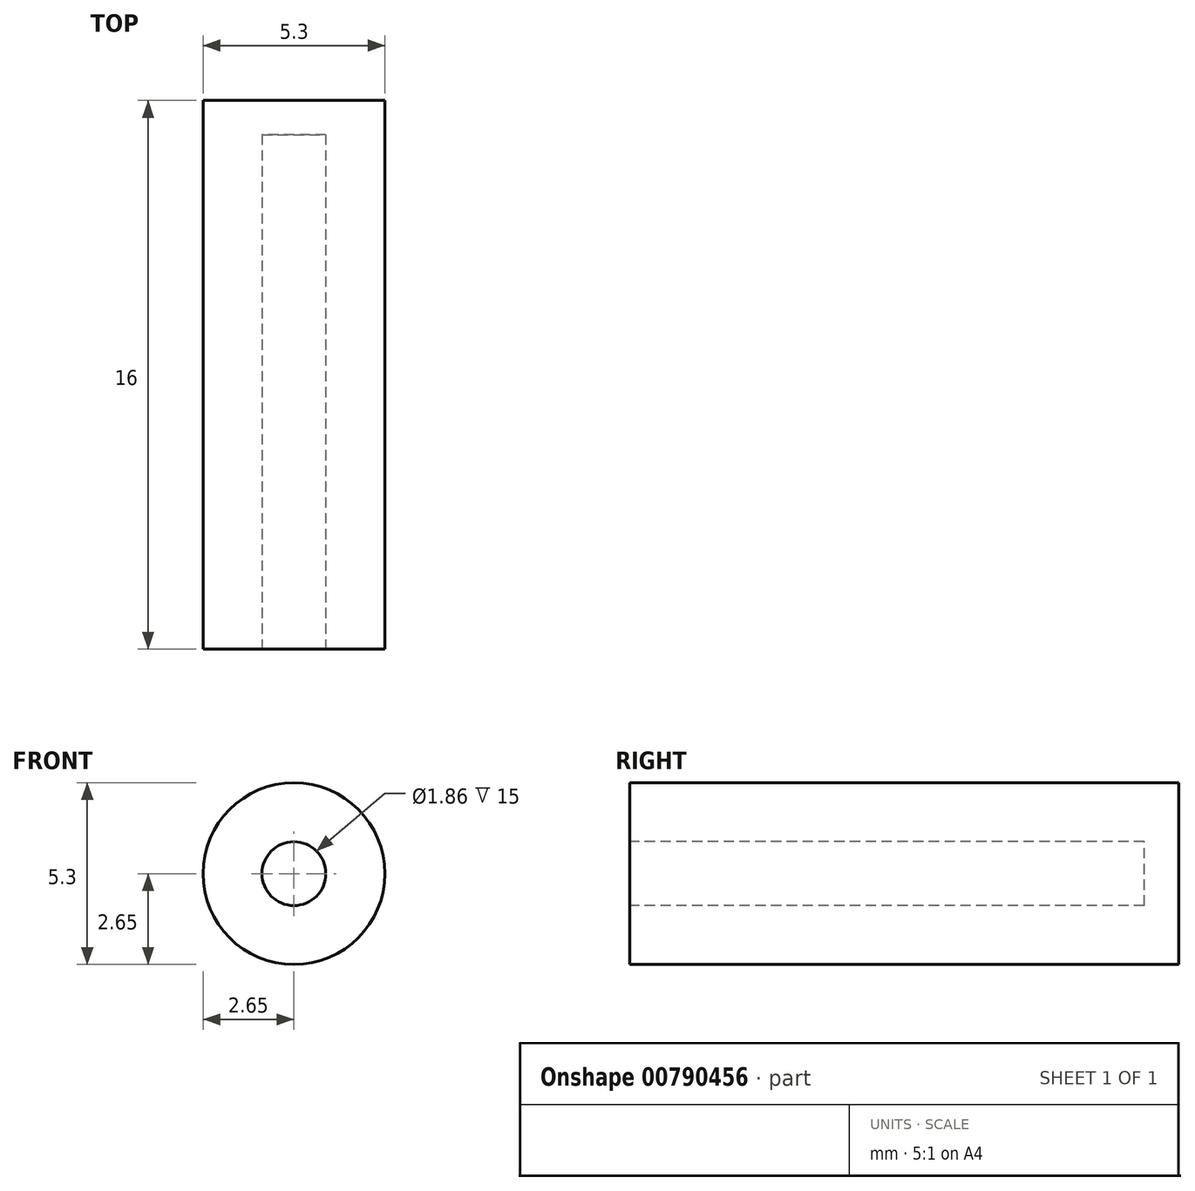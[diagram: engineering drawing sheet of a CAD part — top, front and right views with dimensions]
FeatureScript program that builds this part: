
annotation { "Feature Type Name" : "Feature", "Feature Type Description" : "" }
export const myFeature = defineFeature(function(context is Context, id is Id, definition is map)
    precondition{}
    {
        {
            var Q0;
            Q0=qCreatedBy(makeId("Top.planeOp"),FACE);
            var sketch = newSketch(context, id + "F0", { "sketchPlane" : qUnion([Q0])});
            skLineSegment(sketch, "E0.bottom", {"start": v(0, 52.82) * mm, "end": v(2.65, 52.82) * mm});
            skLineSegment(sketch, "E0.top", {"start": v(0, 51.82) * mm, "end": v(2.65, 51.82) * mm});
            skLineSegment(sketch, "E0.left", {"start": v(0, 52.82) * mm, "end": v(0, 51.82) * mm});
            skLineSegment(sketch, "E0.right", {"start": v(2.65, 52.82) * mm, "end": v(2.65, 51.82) * mm});
            skLineSegment(sketch, "E1", {"start": v(0, 51.82) * mm, "end": v(0, 76.82) * mm, "construction": true});
            skLineSegment(sketch, "E2", {"start": v(0.93, 40.64) * mm, "end": v(0.93, 51.82) * mm});
            skLineSegment(sketch, "E3", {"start": v(0, 36.82) * mm, "end": v(0.02, 36.82) * mm});
            skLineSegment(sketch, "E4.right", {"start": v(2.65, 52.82) * mm, "end": v(2.65, 36.82) * mm});
            skLineSegment(sketch, "E5", {"start": v(0.93, 40.64) * mm, "end": v(0.93, 36.82) * mm});
            skLineSegment(sketch, "E6.trimOffspring", {"start": v(0.93, 36.82) * mm, "end": v(2.65, 36.82) * mm});
            skSolve(sketch);
        }
        {
            var Q0;
            {var subQ1=sQuery(id+"F0.wireOp",EDGE,"E0.bottom");Q0=makeQuery(id+"F0.imprint","IMPRINT",FACE,{"disambiguationData":[TD([[makeQuery(id+"F0.imprint","IMPRINT",EDGE,{"derivedFrom":subQ1}),-1.0]])]});}
            var Q1;
            {var subQ0=sQuery(id+"F0.wireOp",EDGE,"E2");Q1=makeQuery(id+"F0.imprint","IMPRINT",FACE,{"disambiguationData":[TD([[makeQuery(id+"F0.imprint","IMPRINT",EDGE,{"derivedFrom":subQ0}),-1.0]])]});}
            var Q2;
            Q2=sQuery(id+"F0.wireOp",EDGE,"E0.bottom");
            var Q3;
            Q3=sQuery(id+"F0.wireOp",EDGE,"E4.right");
            var Q4;
            Q4=sQuery(id+"F0.wireOp",EDGE,"E0.left");
            var Q5;
            Q5=sQuery(id+"F0.wireOp",EDGE,"E0.top");
            var Q6;
            Q6=sQuery(id+"F0.wireOp",EDGE,"E2");
            var Q7;
            Q7=sQuery(id+"F0.wireOp",EDGE,"E5");
            var Q8;
            Q8=sQuery(id+"F0.wireOp",EDGE,"E6.trimOffspring");
            var Q9;
            Q9=sQuery(id+"F0.wireOp",EDGE,"E1");
            revolve(context, id + "F1", {"surfaceOperationType" : NewSurfaceOperationType.NEW, "entities" : qUnion([Q0, Q1]), "surfaceEntities" : qUnion([Q2, Q3, Q4, Q5, Q6, Q7, Q8]), "axis" : qUnion([Q9]), "revolveType" : RevolveType.FULL});
        }
    });
